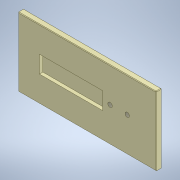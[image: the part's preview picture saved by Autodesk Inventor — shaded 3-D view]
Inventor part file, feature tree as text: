
AUTODESK INVENTOR PART (.ipt)
format: ipt  version: 2021 (Build 250183000, 183)  size: 143,360 bytes
history: native  units: mm
features: other x3, extrude x3, sketch x3, reference x3, thread x2, chamfer x2
ambient origin geometry x8: Origin, YZ Plane, XZ Plane, XY Plane, X Axis, Y Axis, Z Axis, Center Point
bodies: Body1 (feature_tree)
feature tree (16):
  other  "Bryła1"
  extrude  "Wyciągnięcie proste1"  Depth=120.0mm
  extrude  "Wyciągnięcie proste2"  Depth=60.0mm
  extrude  "Wyciągnięcie proste3"  Depth=5.0mm TaperAngle=0.0deg
  thread  "Gwint1"
  thread  "Gwint2"
  chamfer  "Faza2"  Distance=55.0mm
  chamfer  "Faza3"  Distance=15.0mm
  sketch  "Szkic1"
  sketch  "Szkic2"
  reference  "Odniesienie1"
  sketch  "Szkic3"
  reference  "Odniesienie2"
  reference  "Odniesienie3"
  other  "Zespół1"
  other  "tensometr:1"
